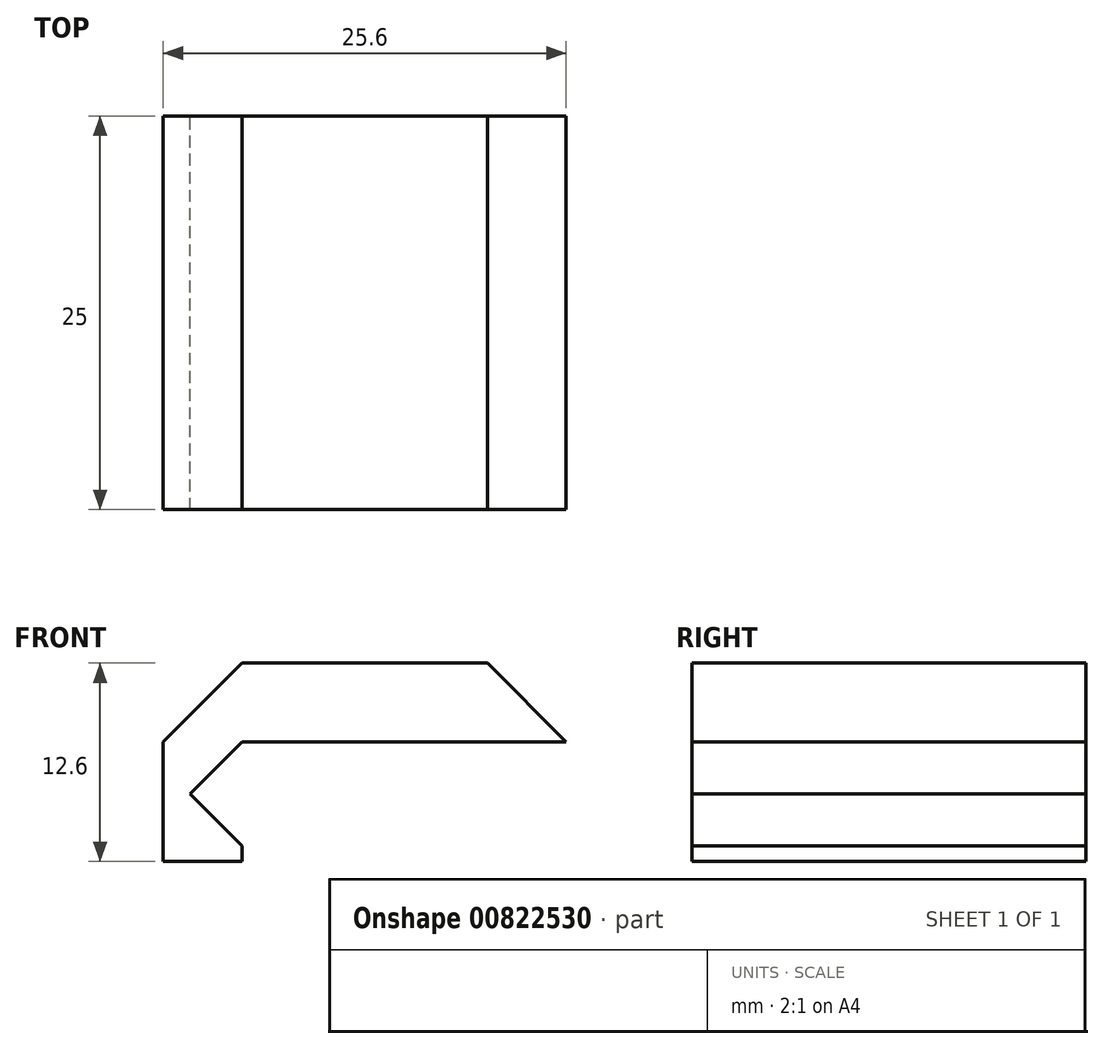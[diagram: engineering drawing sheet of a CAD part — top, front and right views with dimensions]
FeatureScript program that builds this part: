
annotation { "Feature Type Name" : "Feature", "Feature Type Description" : "" }
export const myFeature = defineFeature(function(context is Context, id is Id, definition is map)
    precondition{}
    {
        {
            var Q0;
            Q0=qCreatedBy(makeId("Front.planeOp"),FACE);
            var sketch = newSketch(context, id + "F0", { "sketchPlane" : qUnion([Q0])});
            skLineSegment(sketch, "E0", {"start": v(-7.8, 0) * mm, "end": v(7.8, 0) * mm});
            skLineSegment(sketch, "E1", {"start": v(-7.8, 0) * mm, "end": v(-11.1, -3.3) * mm});
            skLineSegment(sketch, "E2", {"start": v(-11.1, -3.3) * mm, "end": v(15.82, -3.3) * mm, "construction": true});
            skLineSegment(sketch, "E3", {"start": v(-7.8, 0) * mm, "end": v(-7.8, -15.2) * mm, "construction": true});
            skLineSegment(sketch, "E4", {"start": v(7.8, 0) * mm, "end": v(7.8, -14.77) * mm, "construction": true});
            skLineSegment(sketch, "E5", {"start": v(-11.1, -3.3) * mm, "end": v(-7.8, -6.6) * mm});
            skLineSegment(sketch, "E6", {"start": v(-7.8, -6.6) * mm, "end": v(-7.8, -7.6) * mm});
            skLineSegment(sketch, "E7", {"start": v(-7.8, -7.6) * mm, "end": v(-12.8, -7.6) * mm});
            skLineSegment(sketch, "E8", {"start": v(-12.8, -7.6) * mm, "end": v(-12.8, 0) * mm});
            skLineSegment(sketch, "E9", {"start": v(-12.8, 0) * mm, "end": v(-7.8, 5) * mm});
            skLineSegment(sketch, "E10", {"start": v(7.8, 0) * mm, "end": v(12.8, 0) * mm});
            skLineSegment(sketch, "E11", {"start": v(12.8, 0) * mm, "end": v(7.8, 5) * mm});
            skLineSegment(sketch, "E12", {"start": v(7.8, 5) * mm, "end": v(-7.8, 5) * mm});
            skSolve(sketch);
        }
        {
            var Q0;
            Q0 = qSketchRegion(id + "F0", true);
            extrude(context, id + "F1", {"entities" : qUnion([Q0]), "depth" : 25 * mm, "offsetDistance" : 25 * mm});
        }
    });
